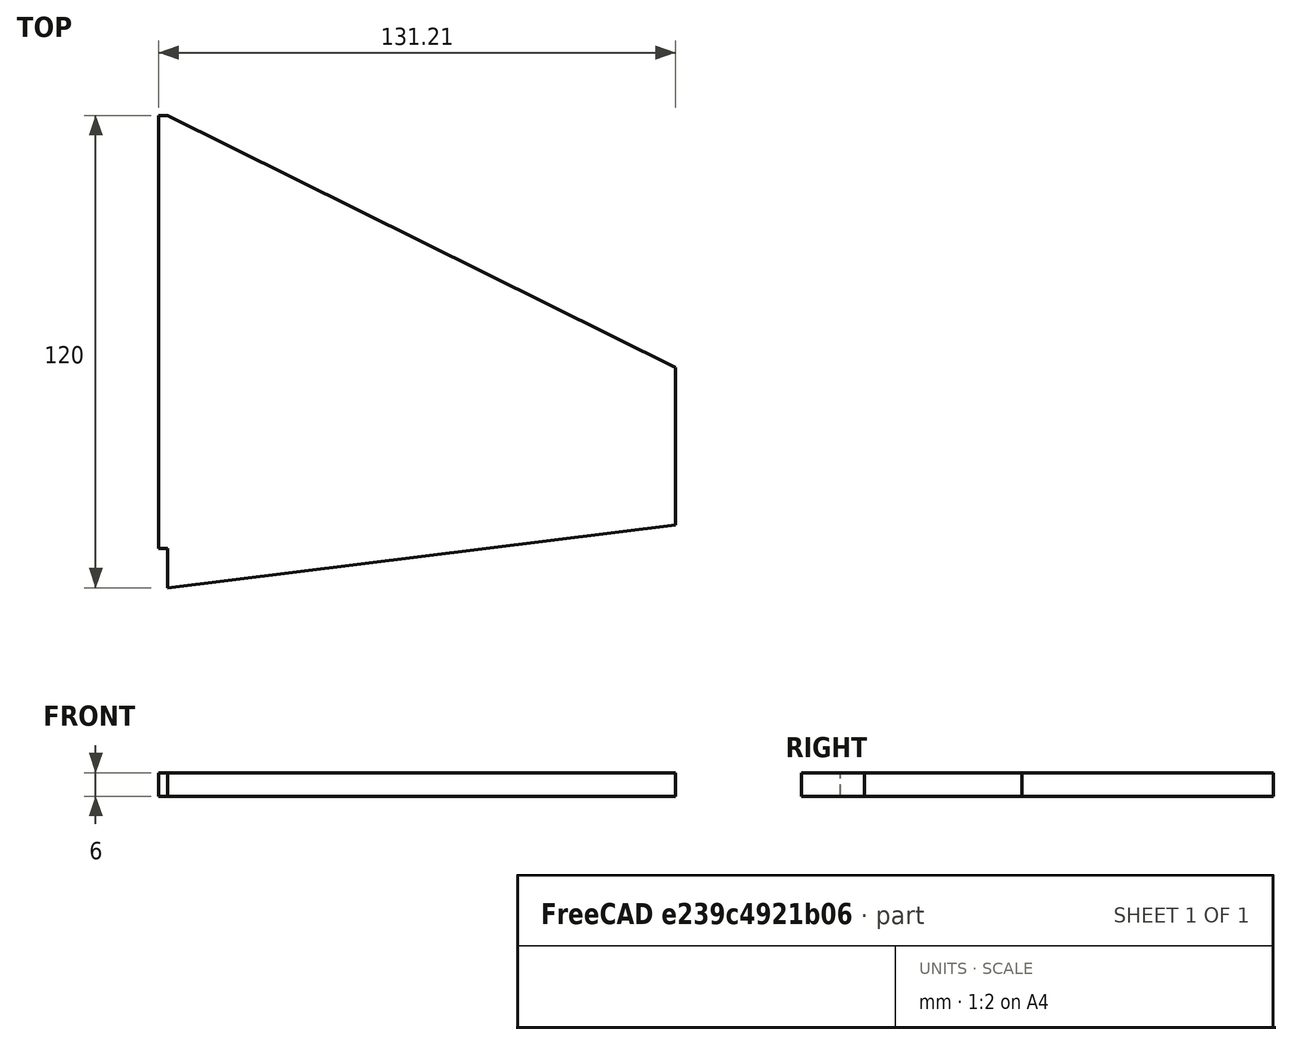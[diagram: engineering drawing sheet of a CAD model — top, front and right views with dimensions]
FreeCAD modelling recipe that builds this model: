
FCSTD DOCUMENT  (FreeCAD 0.18R16093 (Git))
Label: fin
License: All rights reserved
LicenseURL: http://en.wikipedia.org/wiki/All_rights_reserved
objects: Sketcher::SketchObject×1, PartDesign::Pad×1, PartDesign::Body×1
note: 4 computed .brp shape members not serialized (recipe doc carries the construction recipe); baked Part::Feature solids carry a one-line shape summary decoded from their .brp

FEATURE [Sketcher::SketchObject] Sketch
  MapMode = 5
  Support = -> [XY_Plane]
  sketch-geometry (7):
    g0: LineSegment StartX=0 StartY=0 StartZ=0 EndX=6.2 EndY=0 EndZ=0
    g1: LineSegment StartX=6.2 StartY=0 StartZ=0 EndX=6.2 EndY=-10 EndZ=0
    g2: LineSegment StartX=6.2 StartY=-10 StartZ=0 EndX=134.233 EndY=12.5267 EndZ=0
    g3: LineSegment StartX=134.233 StartY=12.5267 StartZ=0 EndX=134.233 EndY=52.5267 EndZ=0
    g4: LineSegment StartX=134.233 StartY=52.5267 StartZ=0 EndX=2.2 EndY=110 EndZ=0
    g5: LineSegment StartX=2.2 StartY=110 StartZ=0 EndX=0 EndY=110 EndZ=0
    g6: LineSegment StartX=0 StartY=110 StartZ=0 EndX=0 EndY=0 EndZ=0
  constraints (20):
    c: Coincident(g0,g1)
    c: Coincident(g1,g2)
    c: Coincident(g2,g3)
    c: Coincident(g3,g4)
    c: Coincident(g4,g5)
    c: Coincident(g5,g6)
    c: Coincident(g6,g0)
    c: Coincident(g0,g-1)
    c: Horizontal(g0)
    c: Vertical(g1)
    c: Vertical(g6)
    c: Horizontal(g5)
    c: DistanceY(g6,g6) = 110
    c: DistanceY(g1,g1) = 10
    c: DistanceX(g0,g0) = 6.2
    c: DistanceX(g5,g5) = 2.2
    c: Vertical(g3)
    c: DistanceY(g3,g3) = 40
    c: Distance(g2) = 130
    c: Distance(g4) = 144
FEATURE [PartDesign::Pad] Pad
  Length = 6
  Length2 = 100
  Profile = -> Sketch
  Type = 0
FEATURE [PartDesign::Body] Body
  Group = -> [Sketch,Pad]
  Origin = -> Origin
  Tip = -> Pad
